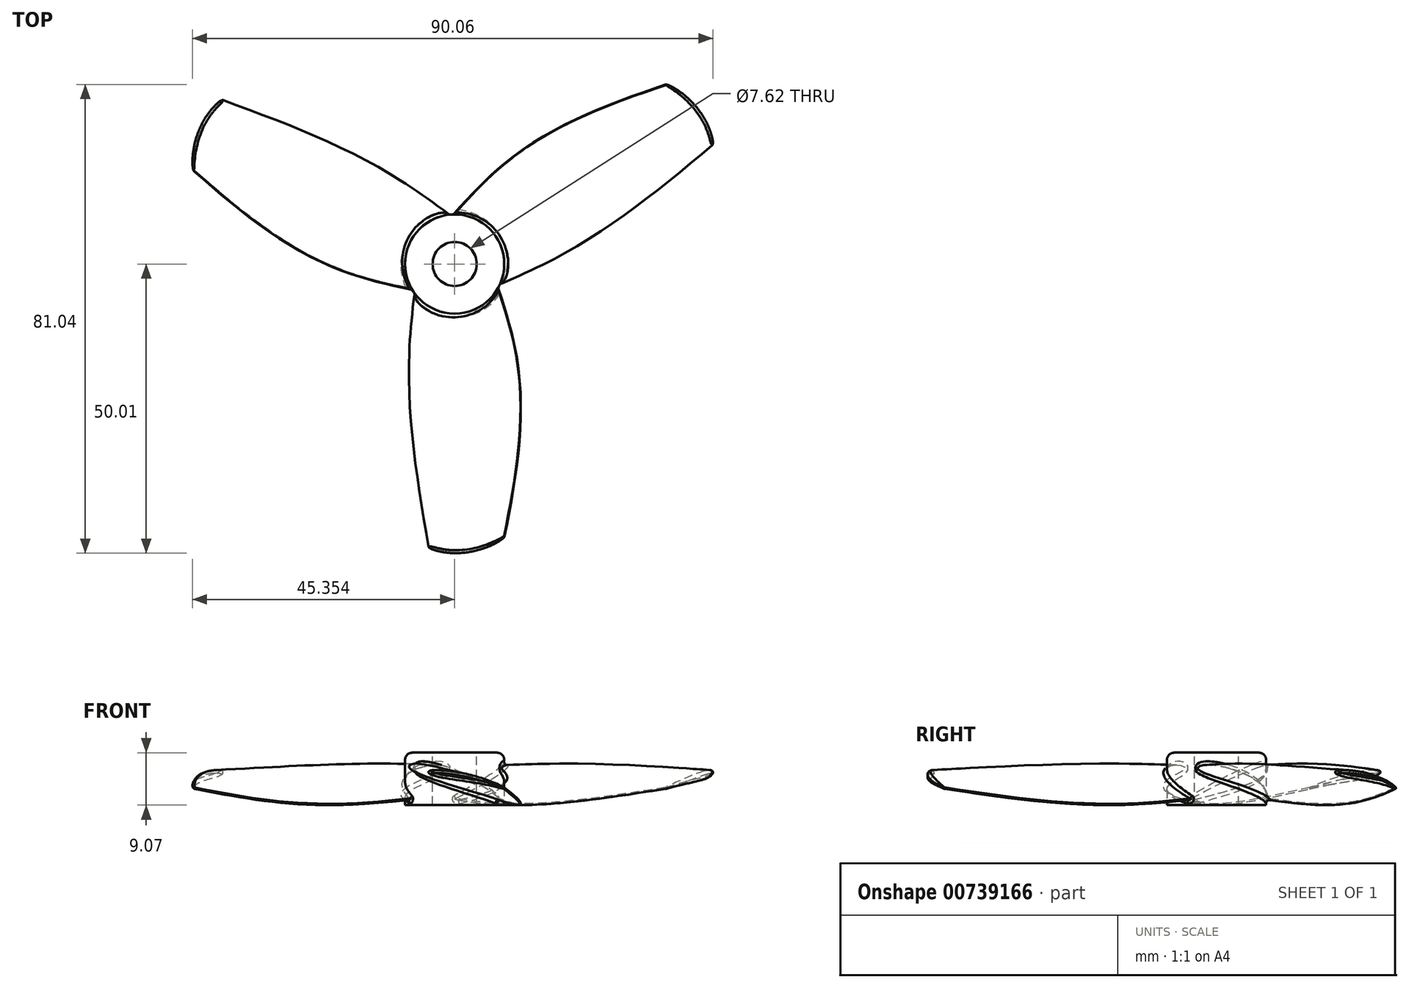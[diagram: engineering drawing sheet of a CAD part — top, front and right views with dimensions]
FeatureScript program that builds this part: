
annotation { "Feature Type Name" : "Feature", "Feature Type Description" : "" }
export const myFeature = defineFeature(function(context is Context, id is Id, definition is map)
    precondition{}
    {
        {
            var Q0;
            Q0=qCreatedBy(makeId("Front.planeOp"),FACE);
            var sketch = newSketch(context, id + "F0", { "sketchPlane" : qUnion([Q0])});
            skLineSegment(sketch, "E0", {"start": v(-25.68, 10.16) * mm, "end": v(0, 0) * mm, "construction": true});
            skLineSegment(sketch, "E1", {"start": v(0, 0) * mm, "end": v(25.68, -10.16) * mm, "construction": true});
            skLineSegment(sketch, "E2", {"start": v(25.68, -10.16) * mm, "end": v(51.36, -20.31) * mm, "construction": true});
            skLineSegment(sketch, "E3", {"start": v(51.36, -20.31) * mm, "end": v(77.03, -30.47) * mm, "construction": true});
            skLineSegment(sketch, "E4", {"start": v(0, 0) * mm, "end": v(3.73, 9.44) * mm, "construction": true});
            skLineSegment(sketch, "E5", {"start": v(-25.68, 10.16) * mm, "end": v(-23.81, 14.88) * mm, "construction": true});
            skFitSpline(sketch, "E6", {"points": [v(-25.68, 10.16) * mm, v(3.73, 9.44) * mm, v(77.03, -30.47) * mm], "startDerivative": vector(15.03, 38) * mm, "endDerivative": vector(104.92, -93.69) * mm});
            skPoint(sketch, "E7", {"position": v(1.87, 4.72) * mm});
            skLineSegment(sketch, "E8", {"start": v(-23.81, 14.88) * mm, "end": v(1.87, 4.72) * mm, "construction": true});
            skLineSegment(sketch, "E9", {"start": v(0, 0) * mm, "end": v(-1.87, -4.72) * mm, "construction": true});
            skLineSegment(sketch, "E10", {"start": v(-25.68, 10.16) * mm, "end": v(-27.54, 5.44) * mm, "construction": true});
            skFitSpline(sketch, "E11", {"points": [v(-25.68, 10.16) * mm, v(-1.87, -4.72) * mm, v(77.03, -30.47) * mm], "startDerivative": vector(-15.23, -38.5) * mm, "endDerivative": vector(121.84, -48.19) * mm});
            skLineSegment(sketch, "E12", {"start": v(51.36, -20.31) * mm, "end": v(55.09, -10.87) * mm, "construction": true});
            skSolve(sketch);
        }
        {
            var Q0;
            Q0=qCreatedBy(makeId("Front.planeOp"),FACE);
            cPlane(context, id + "F1", {"entities" : qUnion([Q0]), "cplaneType" : CPlaneType.OFFSET, "offset" : 125 * mm, "width" : 150 * mm, "height" : 150 * mm});
        }
        {
            var Q0;
            Q0=qCreatedBy(id+"F1.planeOp",FACE);
            var sketch = newSketch(context, id + "F2", { "sketchPlane" : qUnion([Q0])});
            skLineSegment(sketch, "E13", {"start": v(-38.33, 14.06) * mm, "end": v(0, 0) * mm, "construction": true});
            skLineSegment(sketch, "E14", {"start": v(0, 0) * mm, "end": v(38.33, -14.06) * mm, "construction": true});
            skLineSegment(sketch, "E15", {"start": v(38.33, -14.06) * mm, "end": v(76.67, -28.12) * mm, "construction": true});
            skLineSegment(sketch, "E16", {"start": v(76.67, -28.12) * mm, "end": v(115, -42.17) * mm, "construction": true});
            skLineSegment(sketch, "E17", {"start": v(0, 0) * mm, "end": v(4.06, 11.06) * mm, "construction": true});
            skLineSegment(sketch, "E18", {"start": v(-38.33, 14.06) * mm, "end": v(-36.3, 19.59) * mm, "construction": true});
            skFitSpline(sketch, "E19", {"points": [v(-38.33, 14.06) * mm, v(4.06, 11.06) * mm, v(115, -42.17) * mm], "startDerivative": vector(16.44, 44.82) * mm, "endDerivative": vector(163.27, -119.63) * mm});
            skPoint(sketch, "E20", {"position": v(2.03, 5.53) * mm});
            skLineSegment(sketch, "E21", {"start": v(-36.3, 19.59) * mm, "end": v(2.03, 5.53) * mm, "construction": true});
            skLineSegment(sketch, "E22", {"start": v(0, 0) * mm, "end": v(-2.03, -5.53) * mm, "construction": true});
            skLineSegment(sketch, "E23", {"start": v(-38.33, 14.06) * mm, "end": v(-40.36, 8.53) * mm, "construction": true});
            skFitSpline(sketch, "E24", {"points": [v(-38.33, 14.06) * mm, v(-2.03, -5.53) * mm, v(115, -42.17) * mm], "startDerivative": vector(-16.57, -45.19) * mm, "endDerivative": vector(181.7, -66.64) * mm});
            skLineSegment(sketch, "E25", {"start": v(76.67, -28.12) * mm, "end": v(80.72, -17.06) * mm, "construction": true});
            skSolve(sketch);
        }
        {
            var Q0;
            Q0=qCreatedBy(makeId("Front.planeOp"),FACE);
            cPlane(context, id + "F3", {"entities" : qUnion([Q0]), "cplaneType" : CPlaneType.OFFSET, "offset" : 400 * mm, "width" : 150 * mm, "height" : 150 * mm});
        }
        {
            var Q0;
            Q0=qCreatedBy(id+"F3.planeOp",FACE);
            var sketch = newSketch(context, id + "F4", { "sketchPlane" : qUnion([Q0])});
            skLineSegment(sketch, "E26", {"start": v(-10.03, 5.14) * mm, "end": v(16.27, 0) * mm, "construction": true});
            skLineSegment(sketch, "E27", {"start": v(16.27, 0) * mm, "end": v(42.56, -5.14) * mm, "construction": true});
            skLineSegment(sketch, "E28", {"start": v(42.56, -5.14) * mm, "end": v(68.86, -10.28) * mm, "construction": true});
            skLineSegment(sketch, "E29", {"start": v(68.86, -10.28) * mm, "end": v(95.16, -15.42) * mm, "construction": true});
            skLineSegment(sketch, "E30", {"start": v(16.27, 0) * mm, "end": v(17.61, 6.9) * mm, "construction": true});
            skLineSegment(sketch, "E31", {"start": v(-10.03, 5.14) * mm, "end": v(-9.36, 8.59) * mm, "construction": true});
            skFitSpline(sketch, "E32", {"points": [v(-10.03, 5.14) * mm, v(17.61, 6.9) * mm, v(95.16, -15.42) * mm], "startDerivative": vector(5.47, 28.01) * mm, "endDerivative": vector(118.7, -57.28) * mm});
            skPoint(sketch, "E33", {"position": v(16.94, 3.45) * mm});
            skLineSegment(sketch, "E34", {"start": v(-9.36, 8.59) * mm, "end": v(16.94, 3.45) * mm, "construction": true});
            skLineSegment(sketch, "E35", {"start": v(16.27, 0) * mm, "end": v(15.6, -3.45) * mm, "construction": true});
            skLineSegment(sketch, "E36", {"start": v(-10.03, 5.14) * mm, "end": v(-10.7, 1.7) * mm, "construction": true});
            skFitSpline(sketch, "E37", {"points": [v(-10.03, 5.14) * mm, v(15.6, -3.45) * mm, v(95.16, -15.42) * mm], "startDerivative": vector(-5.51, -28.2) * mm, "endDerivative": vector(124.61, -24.36) * mm});
            skLineSegment(sketch, "E38", {"start": v(68.86, -10.28) * mm, "end": v(70.2, -3.38) * mm, "construction": true});
            skSolve(sketch);
        }
        {
            var Q0;
            Q0=qSketchRegion(id+"F0",true);
            var Q1;
            Q1=qSketchRegion(id+"F2",true);
            var Q2;
            Q2=qSketchRegion(id+"F4",true);
            var Q3;
            Q3=sQuery(id+"F0.wireOp",VERTEX,"E6.1.internal");
            var Q4;
            Q4=sQuery(id+"F2.wireOp",VERTEX,"E19.1.internal");
            var Q5;
            Q5=sQuery(id+"F4.wireOp",VERTEX,"E30.end");
            loft(context, id + "F5", {"sheetProfilesArray" : [{ "sheetProfileEntities" : qUnion([Q0]) }, { "sheetProfileEntities" : qUnion([Q1]) }, { "sheetProfileEntities" : qUnion([Q2]) }], "matchConnections" : true, "connections" : [{ "connectionEntities" : qUnion([Q3, Q4, Q5]), "connectionEdgeQueries" : qUnion([]), "connectionEdgeParameters" : [] }]});
        }
        {
            var Q0;
            Q0=qCreatedBy(makeId("Top.planeOp"),FACE);
            var sketch = newSketch(context, id + "F6", { "sketchPlane" : qUnion([Q0])});
            skFitSpline(sketch, "E39", {"points": [v(-55.98, -360.47) * mm, v(39.38, -398.87) * mm, v(142.8, -333.19) * mm], "startDerivative": vector(111.22, -150.8) * mm, "endDerivative": vector(54.24, 145.78) * mm});
            skLineSegment(sketch, "E40", {"start": v(-55.98, -360.47) * mm, "end": v(-55.98, -458.75) * mm});
            skLineSegment(sketch, "E41", {"start": v(142.8, -333.19) * mm, "end": v(142.8, -458.75) * mm});
            skLineSegment(sketch, "E42", {"start": v(142.8, -458.75) * mm, "end": v(-55.98, -458.75) * mm});
            skSolve(sketch);
        }
        {
            var Q0;
            Q0=qSketchRegion(id+"F6",true);
            extrude(context, id + "F7", {"entities" : qUnion([Q0]), "operationType" : NewBodyOperationType.REMOVE, "endBound" : BoundingType.SYMMETRIC, "oppositeDirection" : true, "depth" : 40.17 * mm});
        }
        {
            var Q0;
            Q0=makeQuery(id+"F5.opLoft","SWEPT_EDGE",EDGE,{"disambiguationData":[OSD([sQuery(id+"F2.wireOp",EDGE,"E19"),sQuery(id+"F2.wireOp",EDGE,"E24"),sQuery(id+"F4.wireOp",EDGE,"E32"),sQuery(id+"F4.wireOp",EDGE,"E37")])]});
            fillet(context, id + "F8", {"entities" : qUnion([Q0]), "radius" : 1 * mm, "tangentPropagation" : true, "allowEdgeOverflow" : false});
        }
        {
            var Q0;
            Q0=makeQuery(id+"F7.boolean.opBoolean","COPY",FACE,{"derivedFrom":makeQuery(id+"F7.opExtrude","SWEPT_FACE",FACE,{"disambiguationData":[OSD([sQuery(id+"F6.wireOp",EDGE,"E39")])]})});
            fillet(context, id + "F9", {"entities" : qUnion([Q0]), "radius" : 4 * mm, "tangentPropagation" : true, "allowEdgeOverflow" : false});
        }
        {
            var Q0;
            Q0=qCreatedBy(makeId("Top.planeOp"),FACE);
            var sketch = newSketch(context, id + "F10", { "sketchPlane" : qUnion([Q0])});
            skCircle(sketch, "E43", {"center": v(24.35, 0) * mm, "radius": 68.6 * mm});
            skSolve(sketch);
        }
        {
            var Q0;
            Q0=qSketchRegion(id+"F10",true);
            extrude(context, id + "F11", {"entities" : qUnion([Q0]), "depth" : 32.31 * mm, "hasSecondDirection" : true, "secondDirectionOppositeDirection" : true, "secondDirectionDepth" : 40 * mm});
        }
        {
            var Q0;
            Q0=makeQuery(id+"F5.opLoft","SWEPT_BODY",BODY,{"disambiguationData":[OSD([makeQuery(id+"F0.imprint","IMPRINT",FACE,{"disambiguationData":[TD([[makeQuery(id+"F0.imprint","IMPRINT",EDGE,{"derivedFrom":sQuery(id+"F0.wireOp",EDGE,"E6")}),-1.0]])]}),sQuery(id+"F2.wireOp",EDGE,"E24"),makeQuery(id+"F4.imprint","IMPRINT",FACE,{"disambiguationData":[TD([[makeQuery(id+"F4.imprint","IMPRINT",EDGE,{"derivedFrom":sQuery(id+"F4.wireOp",EDGE,"E32")}),-1.0]])]})])]});
            var Q1;
            Q1=makeQuery(id+"F11.opExtrude","SWEPT_FACE",FACE,{"disambiguationData":[OSD([sQuery(id+"F10.wireOp",EDGE,"E43")])]});
            circularPattern(context, id + "F12", {"entities" : qUnion([Q0]), "axis" : qUnion([Q1]), "angle" : 360 * degree, "instanceCount" : 3, "equalSpace" : true});
        }
        {
            var Q0;
            Q0=makeQuery(id+"F12.opPattern","COPY",BODY,{"derivedFrom":makeQuery(id+"F5.opLoft","SWEPT_BODY",BODY,{"disambiguationData":[OSD([makeQuery(id+"F0.imprint","IMPRINT",FACE,{"disambiguationData":[TD([[makeQuery(id+"F0.imprint","IMPRINT",EDGE,{"derivedFrom":sQuery(id+"F0.wireOp",EDGE,"E6")}),-1.0]])]}),sQuery(id+"F2.wireOp",EDGE,"E24"),makeQuery(id+"F4.imprint","IMPRINT",FACE,{"disambiguationData":[TD([[makeQuery(id+"F4.imprint","IMPRINT",EDGE,{"derivedFrom":sQuery(id+"F4.wireOp",EDGE,"E32")}),-1.0]])]})])]}),"instanceName":"2"});
            var Q1;
            Q1=makeQuery(id+"F5.opLoft","SWEPT_BODY",BODY,{"disambiguationData":[OSD([makeQuery(id+"F0.imprint","IMPRINT",FACE,{"disambiguationData":[TD([[makeQuery(id+"F0.imprint","IMPRINT",EDGE,{"derivedFrom":sQuery(id+"F0.wireOp",EDGE,"E6")}),-1.0]])]}),sQuery(id+"F2.wireOp",EDGE,"E24"),makeQuery(id+"F4.imprint","IMPRINT",FACE,{"disambiguationData":[TD([[makeQuery(id+"F4.imprint","IMPRINT",EDGE,{"derivedFrom":sQuery(id+"F4.wireOp",EDGE,"E32")}),-1.0]])]})])]});
            var Q2;
            Q2=makeQuery(id+"F11.opExtrude","SWEPT_BODY",BODY,{"disambiguationData":[OSD([sQuery(id+"F10.wireOp",EDGE,"E43")])]});
            var Q3;
            Q3=makeQuery(id+"F12.opPattern","COPY",BODY,{"derivedFrom":makeQuery(id+"F5.opLoft","SWEPT_BODY",BODY,{"disambiguationData":[OSD([makeQuery(id+"F0.imprint","IMPRINT",FACE,{"disambiguationData":[TD([[makeQuery(id+"F0.imprint","IMPRINT",EDGE,{"derivedFrom":sQuery(id+"F0.wireOp",EDGE,"E6")}),-1.0]])]}),sQuery(id+"F2.wireOp",EDGE,"E24"),makeQuery(id+"F4.imprint","IMPRINT",FACE,{"disambiguationData":[TD([[makeQuery(id+"F4.imprint","IMPRINT",EDGE,{"derivedFrom":sQuery(id+"F4.wireOp",EDGE,"E32")}),-1.0]])]})])]}),"instanceName":"1"});
            var Q4;
            Q4=makeQuery(id+"F12.opPattern","COPY",BODY,{"derivedFrom":makeQuery(id+"F5.opLoft","SWEPT_BODY",BODY,{"disambiguationData":[OSD([makeQuery(id+"F0.imprint","IMPRINT",FACE,{"disambiguationData":[TD([[makeQuery(id+"F0.imprint","IMPRINT",EDGE,{"derivedFrom":sQuery(id+"F0.wireOp",EDGE,"E6")}),-1.0]])]}),sQuery(id+"F2.wireOp",EDGE,"E24"),makeQuery(id+"F4.imprint","IMPRINT",FACE,{"disambiguationData":[TD([[makeQuery(id+"F4.imprint","IMPRINT",EDGE,{"derivedFrom":sQuery(id+"F4.wireOp",EDGE,"E32")}),-1.0]])]})])]}),"instanceName":"4"});
            var Q5;
            Q5=makeQuery(id+"F12.opPattern","COPY",BODY,{"derivedFrom":makeQuery(id+"F5.opLoft","SWEPT_BODY",BODY,{"disambiguationData":[OSD([makeQuery(id+"F0.imprint","IMPRINT",FACE,{"disambiguationData":[TD([[makeQuery(id+"F0.imprint","IMPRINT",EDGE,{"derivedFrom":sQuery(id+"F0.wireOp",EDGE,"E6")}),-1.0]])]}),sQuery(id+"F2.wireOp",EDGE,"E24"),makeQuery(id+"F4.imprint","IMPRINT",FACE,{"disambiguationData":[TD([[makeQuery(id+"F4.imprint","IMPRINT",EDGE,{"derivedFrom":sQuery(id+"F4.wireOp",EDGE,"E32")}),-1.0]])]})])]}),"instanceName":"3"});
            booleanBodies(context, id + "F13", {"operationType" : BooleanOperationType.UNION, "tools" : qUnion([Q0, Q1, Q2, Q3, Q4, Q5])});
        }
        {
            var Q0;
            Q0=makeQuery(id+"F11.opExtrude","CAP_FACE",FACE,{"disambiguationData":[OSD([sQuery(id+"F10.wireOp",EDGE,"E43")])],"isStart":false});
            var sketch = newSketch(context, id + "F14", { "sketchPlane" : qUnion([Q0])});
            skCircle(sketch, "E44", {"center": v(24.35, 0) * mm, "radius": 30.45 * mm});
            skSolve(sketch);
        }
        {
            var Q0;
            Q0=qSketchRegion(id+"F14",true);
            extrude(context, id + "F15", {"entities" : qUnion([Q0]), "operationType" : NewBodyOperationType.REMOVE, "endBound" : BoundingType.THROUGH_ALL, "oppositeDirection" : true, "depth" : 25 * mm});
        }
        {
            var Q0;
            {var subQ0=sQuery(id+"F0.wireOp",VERTEX,"E6.1.internal");var subQ1=sQuery(id+"F0.wireOp",EDGE,"E6");var subQ2=sQuery(id+"F0.wireOp",EDGE,"E11");var subQ3=sQuery(id+"F2.wireOp",VERTEX,"E19.1.internal");var subQ4=sQuery(id+"F2.wireOp",EDGE,"E19");var subQ5=sQuery(id+"F2.wireOp",EDGE,"E24");Q0=makeQuery(id+"F13.opBoolean","INTERSECT",EDGE,{"derivedFrom":[makeQuery(id+"F11.opExtrude","SWEPT_FACE",FACE,{"disambiguationData":[OSD([sQuery(id+"F10.wireOp",EDGE,"E43")])]}),makeQuery(id+"F12.opPattern","COPY",FACE,{"derivedFrom":makeQuery(id+"F5.opLoft","SWEPT_FACE",FACE,{"disambiguationData":[OSD([subQ0,subQ1,subQ2,subQ3,subQ4,subQ5]),TDD([subQ0,makeQuery(id+"F0.imprint","INTERSECT",VERTEX,{"disambiguationData":[OD(0.0)],"derivedFrom":[subQ1,subQ2]}),makeQuery(id+"F0.imprint","IMPRINT",EDGE,{"derivedFrom":subQ1}),subQ3,makeQuery(id+"F2.imprint","INTERSECT",VERTEX,{"disambiguationData":[OD(0.0)],"derivedFrom":[subQ4,subQ5]}),makeQuery(id+"F2.imprint","IMPRINT",EDGE,{"derivedFrom":subQ4})])]}),"instanceName":"2"})]});}
            var Q1;
            {var subQ0=sQuery(id+"F0.wireOp",VERTEX,"E6.1.internal");var subQ1=sQuery(id+"F0.wireOp",EDGE,"E6");var subQ2=sQuery(id+"F0.wireOp",EDGE,"E11");var subQ3=sQuery(id+"F2.wireOp",VERTEX,"E19.1.internal");var subQ4=sQuery(id+"F2.wireOp",EDGE,"E19");var subQ5=sQuery(id+"F2.wireOp",EDGE,"E24");Q1=makeQuery(id+"F13.opBoolean","INTERSECT",EDGE,{"derivedFrom":[makeQuery(id+"F5.opLoft","SWEPT_FACE",FACE,{"disambiguationData":[OSD([subQ0,subQ1,subQ2,subQ3,subQ4,subQ5]),TDD([subQ0,makeQuery(id+"F0.imprint","INTERSECT",VERTEX,{"disambiguationData":[OD(1.0)],"derivedFrom":[subQ1,subQ2]}),makeQuery(id+"F0.imprint","IMPRINT",EDGE,{"derivedFrom":subQ1}),subQ3,makeQuery(id+"F2.imprint","INTERSECT",VERTEX,{"disambiguationData":[OD(1.0)],"derivedFrom":[subQ4,subQ5]}),makeQuery(id+"F2.imprint","IMPRINT",EDGE,{"derivedFrom":subQ4})])]}),makeQuery(id+"F11.opExtrude","SWEPT_FACE",FACE,{"disambiguationData":[OSD([sQuery(id+"F10.wireOp",EDGE,"E43")])]})]});}
            var Q2;
            {var subQ0=sQuery(id+"F0.wireOp",VERTEX,"E6.1.internal");var subQ1=sQuery(id+"F0.wireOp",EDGE,"E6");var subQ2=sQuery(id+"F0.wireOp",EDGE,"E11");var subQ3=sQuery(id+"F2.wireOp",VERTEX,"E19.1.internal");var subQ4=sQuery(id+"F2.wireOp",EDGE,"E19");var subQ5=sQuery(id+"F2.wireOp",EDGE,"E24");Q2=makeQuery(id+"F13.opBoolean","INTERSECT",EDGE,{"derivedFrom":[makeQuery(id+"F11.opExtrude","SWEPT_FACE",FACE,{"disambiguationData":[OSD([sQuery(id+"F10.wireOp",EDGE,"E43")])]}),makeQuery(id+"F12.opPattern","COPY",FACE,{"derivedFrom":makeQuery(id+"F5.opLoft","SWEPT_FACE",FACE,{"disambiguationData":[OSD([subQ0,subQ1,subQ2,subQ3,subQ4,subQ5]),TDD([subQ0,makeQuery(id+"F0.imprint","INTERSECT",VERTEX,{"disambiguationData":[OD(1.0)],"derivedFrom":[subQ1,subQ2]}),makeQuery(id+"F0.imprint","IMPRINT",EDGE,{"derivedFrom":subQ1}),subQ3,makeQuery(id+"F2.imprint","INTERSECT",VERTEX,{"disambiguationData":[OD(1.0)],"derivedFrom":[subQ4,subQ5]}),makeQuery(id+"F2.imprint","IMPRINT",EDGE,{"derivedFrom":subQ4})])]}),"instanceName":"1"})]});}
            var Q3;
            {var subQ0=sQuery(id+"F0.wireOp",VERTEX,"E6.1.internal");var subQ1=sQuery(id+"F0.wireOp",EDGE,"E6");var subQ2=sQuery(id+"F0.wireOp",EDGE,"E11");var subQ3=sQuery(id+"F2.wireOp",VERTEX,"E19.1.internal");var subQ4=sQuery(id+"F2.wireOp",EDGE,"E19");var subQ5=sQuery(id+"F2.wireOp",EDGE,"E24");Q3=makeQuery(id+"F13.opBoolean","INTERSECT",EDGE,{"derivedFrom":[makeQuery(id+"F11.opExtrude","SWEPT_FACE",FACE,{"disambiguationData":[OSD([sQuery(id+"F10.wireOp",EDGE,"E43")])]}),makeQuery(id+"F12.opPattern","COPY",FACE,{"derivedFrom":makeQuery(id+"F5.opLoft","SWEPT_FACE",FACE,{"disambiguationData":[OSD([subQ0,subQ1,subQ2,subQ3,subQ4,subQ5]),TDD([subQ0,makeQuery(id+"F0.imprint","INTERSECT",VERTEX,{"disambiguationData":[OD(1.0)],"derivedFrom":[subQ1,subQ2]}),makeQuery(id+"F0.imprint","IMPRINT",EDGE,{"derivedFrom":subQ1}),subQ3,makeQuery(id+"F2.imprint","INTERSECT",VERTEX,{"disambiguationData":[OD(1.0)],"derivedFrom":[subQ4,subQ5]}),makeQuery(id+"F2.imprint","IMPRINT",EDGE,{"derivedFrom":subQ4})])]}),"instanceName":"4"})]});}
            var Q4;
            {var subQ0=sQuery(id+"F0.wireOp",VERTEX,"E6.1.internal");var subQ1=sQuery(id+"F0.wireOp",EDGE,"E6");var subQ2=sQuery(id+"F0.wireOp",EDGE,"E11");var subQ3=sQuery(id+"F2.wireOp",VERTEX,"E19.1.internal");var subQ4=sQuery(id+"F2.wireOp",EDGE,"E19");var subQ5=sQuery(id+"F2.wireOp",EDGE,"E24");Q4=makeQuery(id+"F13.opBoolean","INTERSECT",EDGE,{"derivedFrom":[makeQuery(id+"F11.opExtrude","SWEPT_FACE",FACE,{"disambiguationData":[OSD([sQuery(id+"F10.wireOp",EDGE,"E43")])]}),makeQuery(id+"F12.opPattern","COPY",FACE,{"derivedFrom":makeQuery(id+"F5.opLoft","SWEPT_FACE",FACE,{"disambiguationData":[OSD([subQ0,subQ1,subQ2,subQ3,subQ4,subQ5]),TDD([subQ0,makeQuery(id+"F0.imprint","INTERSECT",VERTEX,{"disambiguationData":[OD(0.0)],"derivedFrom":[subQ1,subQ2]}),makeQuery(id+"F0.imprint","IMPRINT",EDGE,{"derivedFrom":subQ1}),subQ3,makeQuery(id+"F2.imprint","INTERSECT",VERTEX,{"disambiguationData":[OD(0.0)],"derivedFrom":[subQ4,subQ5]}),makeQuery(id+"F2.imprint","IMPRINT",EDGE,{"derivedFrom":subQ4})])]}),"instanceName":"3"})]});}
            fillet(context, id + "F16", {"entities" : qUnion([Q0, Q1, Q2, Q3, Q4]), "radius" : 5 * mm, "tangentPropagation" : true, "allowEdgeOverflow" : false});
        }
        {
            var Q0;
            Q0=makeQuery(id+"F11.opExtrude","CAP_EDGE",EDGE,{"disambiguationData":[OSD([sQuery(id+"F10.wireOp",EDGE,"E43")])],"isStart":false});
            fillet(context, id + "F17", {"entities" : qUnion([Q0]), "radius" : 10 * mm, "tangentPropagation" : true, "allowEdgeOverflow" : false});
        }
        {
            var Q0;
            Q0=makeQuery(id+"F12.opPattern","COPY",BODY,{"derivedFrom":makeQuery(id+"F5.opLoft","SWEPT_BODY",BODY,{"disambiguationData":[OSD([makeQuery(id+"F0.imprint","IMPRINT",FACE,{"disambiguationData":[TD([[makeQuery(id+"F0.imprint","IMPRINT",EDGE,{"derivedFrom":sQuery(id+"F0.wireOp",EDGE,"E6")}),-1.0]])]}),sQuery(id+"F2.wireOp",EDGE,"E19"),makeQuery(id+"F4.imprint","IMPRINT",FACE,{"disambiguationData":[TD([[makeQuery(id+"F4.imprint","IMPRINT",EDGE,{"derivedFrom":sQuery(id+"F4.wireOp",EDGE,"E32")}),-1.0]])]})])]}),"instanceName":"2"});
            var Q1;
            Q1=sQuery(id+"F0.wireOp",VERTEX,"E7");
            transform(context, id + "F18", {"entities" : qUnion([Q0]), "transformType" : TransformType.SCALE_UNIFORMLY, "scale" : .1, "scalePoint" : qUnion([Q1]), "makeCopy" : false});
        }
        {
            var Q0;
            Q0=makeQuery(id+"F12.opPattern","COPY",BODY,{"derivedFrom":makeQuery(id+"F5.opLoft","SWEPT_BODY",BODY,{"disambiguationData":[OSD([makeQuery(id+"F0.imprint","IMPRINT",FACE,{"disambiguationData":[TD([[makeQuery(id+"F0.imprint","IMPRINT",EDGE,{"derivedFrom":sQuery(id+"F0.wireOp",EDGE,"E6")}),-1.0]])]}),sQuery(id+"F2.wireOp",EDGE,"E19"),makeQuery(id+"F4.imprint","IMPRINT",FACE,{"disambiguationData":[TD([[makeQuery(id+"F4.imprint","IMPRINT",EDGE,{"derivedFrom":sQuery(id+"F4.wireOp",EDGE,"E32")}),-1.0]])]})])]}),"instanceName":"2"});
            var Q1;
            Q1=sQuery(id+"F14.wireOp",VERTEX,"E44.center");
            transform(context, id + "F19", {"entities" : qUnion([Q0]), "transformType" : TransformType.SCALE_UNIFORMLY, "scale" : 1.25, "scalePoint" : qUnion([Q1]), "makeCopy" : false});
        }
    });
